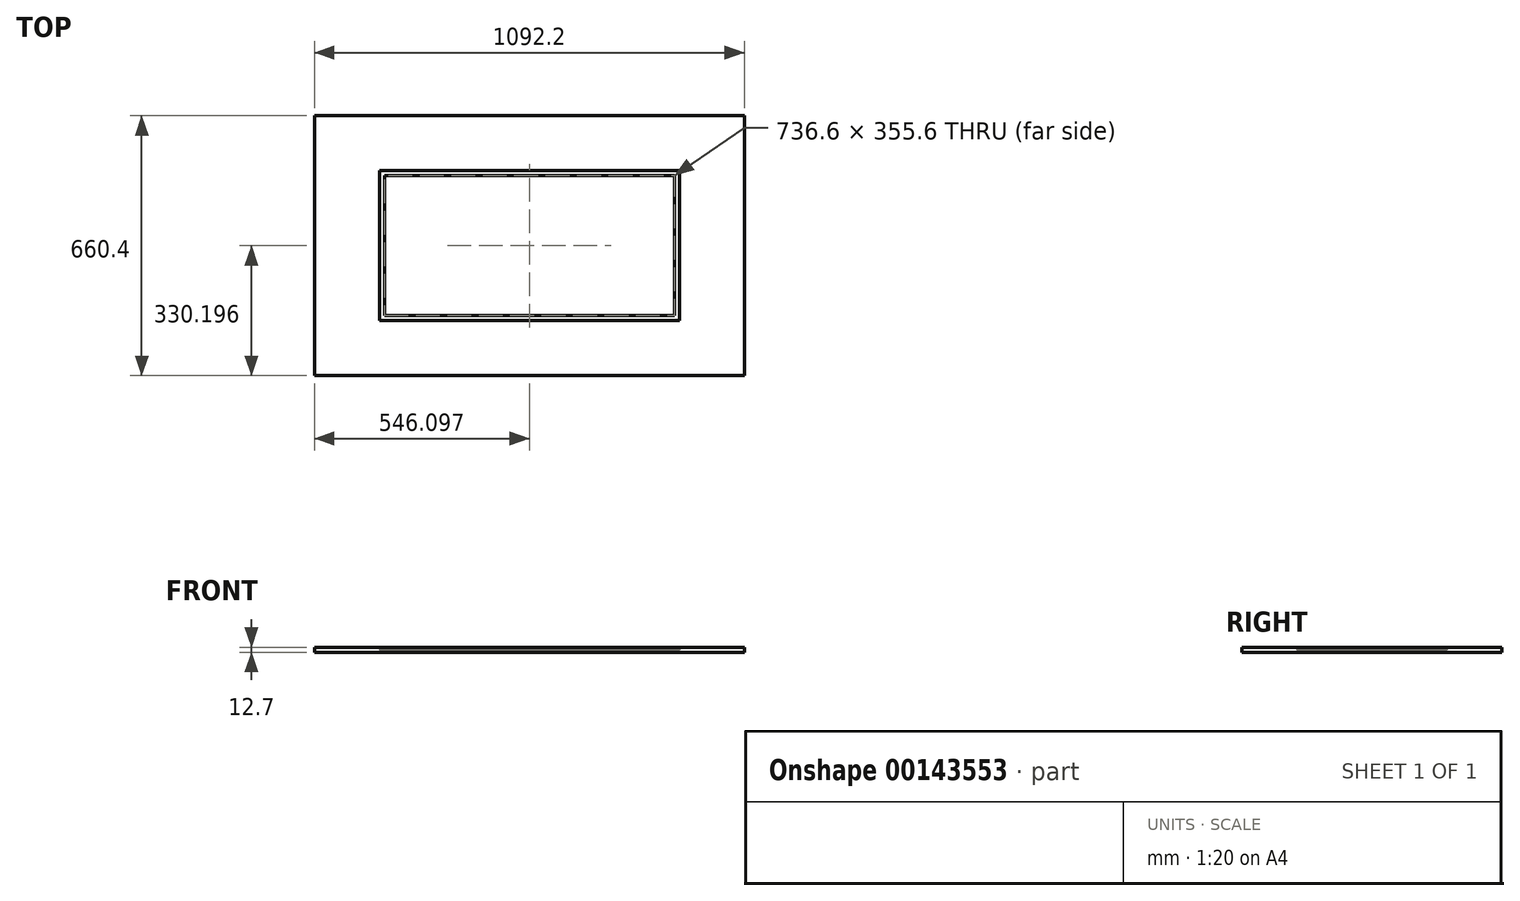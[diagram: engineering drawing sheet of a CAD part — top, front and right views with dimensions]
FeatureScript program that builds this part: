
annotation { "Feature Type Name" : "Feature", "Feature Type Description" : "" }
export const myFeature = defineFeature(function(context is Context, id is Id, definition is map)
    precondition{}
    {
        {
            var Q0;
            Q0=qCreatedBy(makeId("Top.planeOp"),FACE);
            var sketch = newSketch(context, id + "F0", { "sketchPlane" : qUnion([Q0])});
            skLineSegment(sketch, "E0.bottom", {"start": v(-1046.88, 614.07) * mm, "end": v(45.32, 614.07) * mm});
            skLineSegment(sketch, "E0.top", {"start": v(-1046.88, -46.33) * mm, "end": v(45.32, -46.33) * mm});
            skLineSegment(sketch, "E0.left", {"start": v(-1046.88, 614.07) * mm, "end": v(-1046.88, -46.33) * mm});
            skLineSegment(sketch, "E0.right", {"start": v(45.32, 614.07) * mm, "end": v(45.32, -46.33) * mm});
            skLineSegment(sketch, "E1.bottom", {"start": v(-881.78, 474.37) * mm, "end": v(-119.78, 474.37) * mm});
            skLineSegment(sketch, "E1.top", {"start": v(-881.78, 93.37) * mm, "end": v(-119.78, 93.37) * mm});
            skLineSegment(sketch, "E1.left", {"start": v(-881.78, 474.37) * mm, "end": v(-881.78, 93.37) * mm});
            skLineSegment(sketch, "E1.right", {"start": v(-119.78, 474.37) * mm, "end": v(-119.78, 93.37) * mm});
            skLineSegment(sketch, "E2", {"start": v(-881.78, 474.37) * mm, "end": v(-1046.88, 474.37) * mm, "construction": true});
            skLineSegment(sketch, "E3", {"start": v(-119.78, 474.37) * mm, "end": v(45.32, 474.37) * mm, "construction": true});
            skLineSegment(sketch, "E4", {"start": v(-881.78, 474.37) * mm, "end": v(-881.78, 614.07) * mm, "construction": true});
            skLineSegment(sketch, "E5.bottom", {"start": v(-869.08, 461.67) * mm, "end": v(-132.48, 461.67) * mm});
            skLineSegment(sketch, "E5.top", {"start": v(-869.08, 106.07) * mm, "end": v(-132.48, 106.07) * mm});
            skLineSegment(sketch, "E5.left", {"start": v(-869.08, 461.67) * mm, "end": v(-869.08, 106.07) * mm});
            skLineSegment(sketch, "E5.right", {"start": v(-132.48, 461.67) * mm, "end": v(-132.48, 106.07) * mm});
            skLineSegment(sketch, "E6", {"start": v(-132.48, 106.07) * mm, "end": v(-132.48, 93.37) * mm, "construction": true});
            skLineSegment(sketch, "E7", {"start": v(-132.48, 106.07) * mm, "end": v(-119.78, 106.07) * mm, "construction": true});
            skSolve(sketch);
        }
        {
            var Q0;
            Q0=makeQuery(id+"F0.imprint","IMPRINT",FACE,{"disambiguationData":[TD([[makeQuery(id+"F0.imprint","IMPRINT",EDGE,{"derivedFrom":sQuery(id+"F0.wireOp",EDGE,"E0.bottom")}),-1.0]])]});
            var Q1;
            Q1=makeQuery(id+"F0.imprint","IMPRINT",FACE,{"disambiguationData":[TD([[makeQuery(id+"F0.imprint","IMPRINT",EDGE,{"derivedFrom":sQuery(id+"F0.wireOp",EDGE,"E1.bottom")}),-1.0]])]});
            extrude(context, id + "F1", {"entities" : qUnion([Q0, Q1]), "depth" : 6.35 * mm});
        }
        {
            var Q0;
            Q0=makeQuery(id+"F0.imprint","IMPRINT",FACE,{"disambiguationData":[TD([[makeQuery(id+"F0.imprint","IMPRINT",EDGE,{"derivedFrom":sQuery(id+"F0.wireOp",EDGE,"E0.bottom")}),-1.0]])]});
            extrude(context, id + "F2", {"entities" : qUnion([Q0]), "operationType" : NewBodyOperationType.ADD, "depth" : 12.7 * mm});
        }
    });
